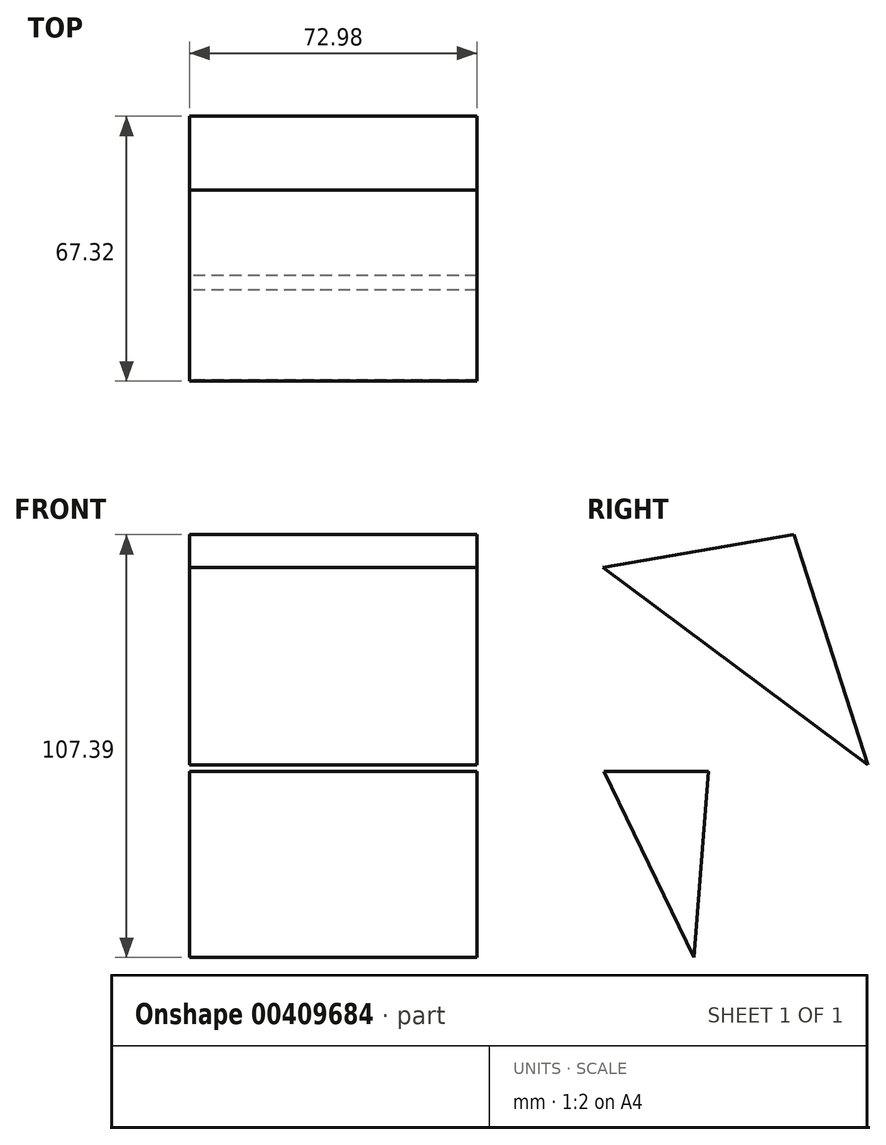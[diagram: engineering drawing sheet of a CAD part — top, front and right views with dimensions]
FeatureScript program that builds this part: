
annotation { "Feature Type Name" : "Feature", "Feature Type Description" : "" }
export const myFeature = defineFeature(function(context is Context, id is Id, definition is map)
    precondition{}
    {
        {
            var Q0;
            Q0=qCreatedBy(makeId("Right.planeOp"),FACE);
            var sketch = newSketch(context, id + "F0", { "sketchPlane" : qUnion([Q0])});
            skLineSegment(sketch, "E0", {"start": v(21.73, 60.15) * mm, "end": v(40.5, 1.6) * mm});
            skLineSegment(sketch, "E1", {"start": v(40.5, 1.6) * mm, "end": v(-43.2, 64.1) * mm});
            skLineSegment(sketch, "E2", {"start": v(-43.2, 64.1) * mm, "end": v(-26.8, 51.86) * mm});
            skLineSegment(sketch, "E3", {"start": v(-44.71, 0) * mm, "end": v(0, 0) * mm});
            skLineSegment(sketch, "E4", {"start": v(0, 0) * mm, "end": v(-3.6, -47.24) * mm});
            skLineSegment(sketch, "E5", {"start": v(-3.6, -47.24) * mm, "end": v(-34.62, 16.8) * mm});
            skLineSegment(sketch, "E6", {"start": v(-26.8, 51.86) * mm, "end": v(21.73, 60.15) * mm});
            skSolve(sketch);
        }
        {
            var Q0;
            Q0=makeQuery(id+"F0.imprint","IMPRINT",FACE,{"disambiguationData":[TD([[makeQuery(id+"F0.imprint","IMPRINT",EDGE,{"derivedFrom":sQuery(id+"F0.wireOp",EDGE,"E0")}),-1.0]])]});
            var Q1;
            {var subQ0=sQuery(id+"F0.wireOp",EDGE,"E4");Q1=makeQuery(id+"F0.imprint","IMPRINT",FACE,{"disambiguationData":[TD([[makeQuery(id+"F0.imprint","IMPRINT",EDGE,{"derivedFrom":subQ0}),-1.0]])]});}
            extrude(context, id + "F1", {"entities" : qUnion([Q0, Q1]), "depth" : 72.98 * mm});
        }
    });
